# Revit family: PUM-01
name_source: partatom
category: Aparatos sanitarios
revit_build: Autodesk Revit 2016 (Build: 20150220_1215(x64)
units: mm (PartAtom-declared; Revit-internal decimal feet)

## family parameters
Compartido = No
Corte con vacíos al cargar = No
Cota de conector redondo = Diámetro de uso
Número OmniClass = 23.45.00.00
Punto de cálculo de habitación = No
Se basa en plano de trabajo = No
Siempre vertical = Sí
Tipo de pieza = Normal
Título OmniClass = Sanitary, Laundry, and Cleaning Equipment

## types (1)
- PUM-01
    Brass Chromed = Brass
    Comentarios de tipo = Special Products
    Descripción = Urinal For Pressure Low Push Valve
    Fabricante = HELVEX
    Features = To Be Used With Ø ¾" (19 mm) Spud
    Inlet Threads = ½" - 14 NPSM
    Max. Working Pressure = 14.2 psi
    Maximum Consumption = 0.26 gpf
    Min. Working Pressure = 3.6 psi
    Modelo = PUM-01
    Total Depth = 4"
    Total Height = 11"
    Total Width = 3"

## geometry (parser evidence)
native form markers: Sweep x2
no freeform markers — native parametric forms only
